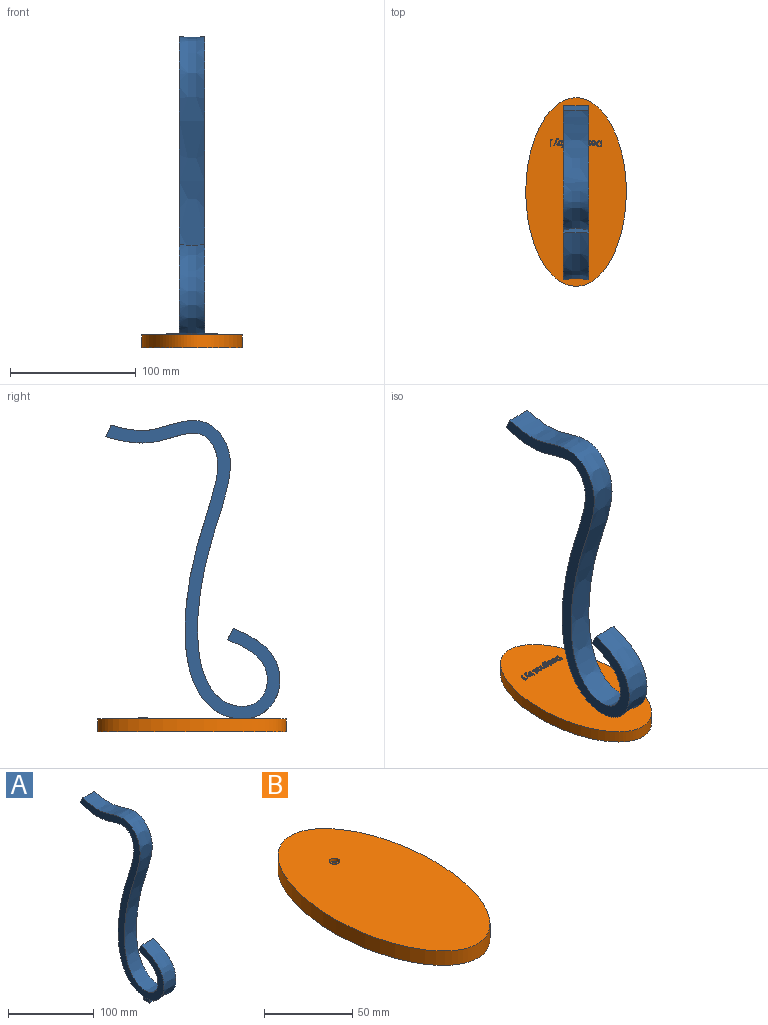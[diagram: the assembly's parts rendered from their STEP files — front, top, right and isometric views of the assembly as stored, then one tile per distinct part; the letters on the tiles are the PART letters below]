
ASSEMBLY  parts=2 mates=1
PART A: 21 faces, bbox 21x139.8x244.8 mm
  f0: plane 16.04x7.22mm, normal (0,-1,0), area 96.4mm2, adj f2,f8,f10,f11,f12,f13,f14,f15
  f1: cylinder r=1.5mm len=3.4mm, axis (0,0,-1), area 32mm2, adj f11,f14
  f2: bspline ~228.79x138.81mm, area 8693.5mm2, adj f0,f3,f5,f6,f7,f8,f9,f10
  f3: plane 238.63x139.71mm, normal (1,0,0), area 4560.6mm2, adj f2,f4,f6,f7
  f4: bspline ~228.74x126mm, area 8298.4mm2, adj f3,f5,f6,f7
  f5: plane 238.85x139.68mm, normal (-1,0,0), area 4534.9mm2, adj f2,f4,f6,f7
  f6: plane 20.02x9.13mm, normal (0,0.91,0.42), area 179.9mm2, adj f2,f3,f4,f5
  f7: plane 20.02x9mm, normal (0,0.89,0.45), area 179.9mm2, adj f2,f3,f4,f5
  f8: plane 10.05x6.7mm, normal (1,0,0), area 64.1mm2, adj f0,f2,f9,f11
  f9: plane 16.26x7.42mm, normal (0,1,0), area 111.7mm2, adj f2,f8,f10,f11
  f10: plane 10.05x6.7mm, normal (-1,0,0), area 64.1mm2, adj f0,f2,f9,f11
  f11: plane 16x10mm, normal (0,0,-1), area 152.9mm2, adj f0,f1,f8,f9,f10
  f12: plane 5.8x2.6mm, normal (-1,0,0), area 15.1mm2, adj f0,f14,f15,f16
  f13: plane 5.8x2.6mm, normal (1,0,0), area 15.1mm2, adj f0,f14,f15,f18
  f14: plane 8x6mm, normal (0,0,1), area 38.1mm2, adj f0,f1,f12,f13,f16,f17,f18
  f15: plane 8x6mm, normal (0,0,-1), area 38.1mm2, adj f0,f12,f13,f16,f17,f18,f19
  f16: plane 2.6x2.2mm, normal (-0.87,-0.5,0), area 6.6mm2, adj f12,f14,f15,f17
  f17: plane 3.46x2.6mm, normal (0,-1,0), area 9mm2, adj f14,f15,f16,f18
  f18: plane 2.6x2.2mm, normal (0.87,-0.5,0), area 6.6mm2, adj f13,f14,f15,f17
  f19: cylinder r=1.5mm len=3mm, axis (0,0,-1), area 28.3mm2, adj f15,f20
  f20: plane 3x3mm, normal (0,0,-1), area 7.1mm2, adj f19
PART B: 253 faces, bbox 80x150x11 mm
  f0: plane 150x80mm, normal (0,0,-1), area 9163.2mm2, adj f2,f3,f4,f5,f6,f17,f18,f19
  f1: cylinder r=1.5mm len=3mm, axis (0,0,1), area 18.8mm2, adj f8,f10
  f2: plane 10.8x6mm, normal (1,0,0), area 64.8mm2, adj f0,f3,f6,f8
  f3: plane 16.4x6mm, normal (0,-1,0), area 98.4mm2, adj f0,f2,f4,f8
  f4: plane 10.8x6mm, normal (-1,0,0), area 64.8mm2, adj f0,f3,f6,f8
  f5: extruded ~150x80mm, area 3697.1mm2, adj f0,f7
  f6: plane 16.4x6mm, normal (0,1,0), area 98.4mm2, adj f0,f2,f4,f8
  f7: plane 150x80mm, normal (0,0,1), area 9396.5mm2, adj f5,f9
  f8: plane 16.4x10.8mm, normal (0,0,-1), area 170.1mm2, adj f1,f2,f3,f4,f6
  f9: cylinder r=3mm len=6mm, axis (0,0,1), area 37.7mm2, adj f7,f10
  f10: plane 6x6mm, normal (0,0,1), area 21.2mm2, adj f1,f9
  f11: extruded ~1.42x1mm, area 1.5mm2, adj f12,f24,f25,f26
  f12: extruded ~1.46x1mm, area 1.6mm2, adj f11,f13,f25,f26
  f13: extruded ~1.5x1mm, area 1.6mm2, adj f12,f14,f25,f26
  f14: plane 1x0.68mm, normal (0,1,0), area 0.7mm2, adj f13,f15,f25,f26
  f15: plane 3.84x1mm, normal (-1,0,0), area 3.8mm2, adj f14,f16,f25,f26
  f16: plane 1x0.81mm, normal (0,-1,0), area 0.8mm2, adj f15,f24,f25,f26
  f17: extruded ~1.82x1mm, area 2mm2, adj f0,f18,f23,f25
  f18: extruded ~1.74x1mm, area 1.9mm2, adj f0,f17,f19,f25
  f19: extruded ~1.74x1mm, area 1.9mm2, adj f0,f18,f20,f25
  f20: plane 1.47x1mm, normal (0,1,0), area 1.5mm2, adj f0,f19,f21,f25
  f21: plane 4.81x1mm, normal (1,0,0), area 4.8mm2, adj f0,f20,f22,f25
  f22: plane 1.33x1mm, normal (0,-1,0), area 1.3mm2, adj f0,f21,f23,f25
  f23: extruded ~1.86x1mm, area 2mm2, adj f0,f17,f22,f25
  f24: extruded ~1.4x1mm, area 1.5mm2, adj f11,f16,f25,f26
  f25: plane 4.81x3.84mm, normal (0,0,-1), area 7.3mm2, adj f11,f12,f13,f14,f15,f16,f17,f18
  f26: plane 3.84x2.69mm, normal (0,0,-1), area 9.1mm2, adj f11,f12,f13,f14,f15,f16,f24
  f27: extruded ~1x0.69mm, area 0.8mm2, adj f28,f45,f46,f47
  f28: extruded ~1x0.66mm, area 0.7mm2, adj f27,f29,f46,f47
  f29: extruded ~1x0.79mm, area 0.8mm2, adj f28,f30,f46,f47
  f30: plane 1.89x1mm, normal (0,1,0), area 1.9mm2, adj f29,f45,f46,f47
  f31: extruded ~1.26x1mm, area 1.4mm2, adj f0,f32,f44,f46
  f32: extruded ~1x0.62mm, area 0.6mm2, adj f0,f31,f33,f46
  f33: extruded ~1x0.55mm, area 0.6mm2, adj f0,f32,f34,f46
  f34: plane 1x0.49mm, normal (-1,0,0), area 0.5mm2, adj f0,f33,f35,f46
  f35: extruded ~1.15x1mm, area 1.2mm2, adj f0,f34,f36,f46
  f36: extruded ~1x0.86mm, area 0.9mm2, adj f0,f35,f37,f46
  f37: extruded ~1x0.96mm, area 1mm2, adj f0,f36,f38,f46
  f38: plane 2.48x1mm, normal (0,-1,0), area 2.5mm2, adj f0,f37,f39,f46
  f39: plane 1x0.35mm, normal (-1,0,0), area 0.3mm2, adj f0,f38,f40,f46
  f40: extruded ~1.18x1mm, area 1.3mm2, adj f0,f39,f41,f46
  f41: extruded ~1.07x1mm, area 1.2mm2, adj f0,f40,f42,f46
  f42: extruded ~1.15x1mm, area 1.3mm2, adj f0,f41,f43,f46
  f43: extruded ~1.39x1mm, area 1.5mm2, adj f0,f42,f44,f46
  f44: extruded ~1.35x1mm, area 1.5mm2, adj f0,f31,f43,f46
  f45: extruded ~1x0.78mm, area 0.9mm2, adj f27,f30,f46,f47
  f46: plane 3.74x3.05mm, normal (0,0,-1), area 5.2mm2, adj f27,f28,f29,f30,f31,f32,f33,f34
  f47: plane 1.89x1.07mm, normal (0,0,-1), area 1.6mm2, adj f27,f28,f29,f30,f45
  f48: extruded ~1x0.78mm, area 0.9mm2, adj f0,f49,f72,f73
  f49: extruded ~1x0.6mm, area 0.7mm2, adj f0,f48,f50,f73
  f50: extruded ~1x0.87mm, area 1mm2, adj f0,f49,f51,f73
  f51: extruded ~1x0.63mm, area 0.7mm2, adj f0,f50,f52,f73
  f52: extruded ~1x0.24mm, area 0.3mm2, adj f0,f51,f53,f73
  f53: extruded ~1x0.25mm, area 0.3mm2, adj f0,f52,f54,f73
  f54: extruded ~1x0.34mm, area 0.4mm2, adj f0,f53,f55,f73
  f55: extruded ~1x0.59mm, area 0.6mm2, adj f0,f54,f56,f73
  f56: extruded ~1x0.98mm, area 1mm2, adj f0,f55,f57,f73
  f57: plane 1x0.44mm, normal (-0.92,-0.4,0), area 0.5mm2, adj f0,f56,f58,f73
  f58: extruded ~1.14x1mm, area 1.2mm2, adj f0,f57,f59,f73
  f59: extruded ~1x0.98mm, area 1mm2, adj f0,f58,f60,f73
  f60: extruded ~1x0.7mm, area 0.8mm2, adj f0,f59,f61,f73
  f61: extruded ~1x0.42mm, area 0.4mm2, adj f0,f60,f62,f73
  f62: extruded ~1x0.32mm, area 0.5mm2, adj f0,f61,f63,f73
  f63: extruded ~1x0.72mm, area 0.8mm2, adj f0,f62,f64,f73
  f64: extruded ~1x0.71mm, area 0.8mm2, adj f0,f63,f65,f73
  f65: extruded ~1x0.36mm, area 0.4mm2, adj f0,f64,f66,f73
  f66: extruded ~1x0.42mm, area 0.5mm2, adj f0,f65,f67,f73
  f67: extruded ~1x0.66mm, area 0.7mm2, adj f0,f66,f68,f73
  f68: extruded ~1x0.57mm, area 0.6mm2, adj f0,f67,f69,f73
  f69: extruded ~1x0.56mm, area 0.6mm2, adj f0,f68,f70,f73
  f70: plane 1x0.51mm, normal (1,0,0), area 0.5mm2, adj f0,f69,f71,f73
  f71: extruded ~1.12x1mm, area 1.2mm2, adj f0,f70,f72,f73
  f72: extruded ~1.05x1mm, area 1.1mm2, adj f0,f48,f71,f73
  f73: plane 3.74x2.56mm, normal (0,0,-1), area 4mm2, adj f48,f49,f50,f51,f52,f53,f54,f55
  f74: plane 1x0.55mm, normal (0,-1,0), area 0.5mm2, adj f0,f75,f77,f78
  f75: plane 3.61x1mm, normal (-1,0,0), area 3.6mm2, adj f0,f74,f76,f78
  f76: plane 1x0.55mm, normal (0,1,0), area 0.5mm2, adj f0,f75,f77,f78
  f77: plane 3.61x1mm, normal (1,0,0), area 3.6mm2, adj f0,f74,f76,f78
  f78: plane 3.61x0.55mm, normal (0,0,-1), area 2mm2, adj f74,f75,f76,f77
  f79: extruded ~1x0.28mm, area 0.3mm2, adj f0,f80,f86,f87
  f80: extruded ~1x0.28mm, area 0.3mm2, adj f0,f79,f81,f87
  f81: extruded ~1x0.23mm, area 0.3mm2, adj f0,f80,f82,f87
  f82: extruded ~1x0.23mm, area 0.3mm2, adj f0,f81,f83,f87
  f83: extruded ~1x0.28mm, area 0.3mm2, adj f0,f82,f84,f87
  f84: extruded ~1x0.27mm, area 0.3mm2, adj f0,f83,f85,f87
  f85: extruded ~1x0.23mm, area 0.2mm2, adj f0,f84,f86,f87
  f86: extruded ~1x0.23mm, area 0.3mm2, adj f0,f79,f85,f87
  f87: plane 0.73x0.65mm, normal (0,0,-1), area 0.4mm2, adj f79,f80,f81,f82,f83,f84,f85,f86
  f88: extruded ~1x0.57mm, area 0.6mm2, adj f89,f131,f132,f134
  f89: extruded ~1x0.62mm, area 0.7mm2, adj f88,f90,f132,f134
  f90: extruded ~1x0.59mm, area 0.6mm2, adj f89,f91,f132,f134
  f91: extruded ~1x0.81mm, area 1.3mm2, adj f90,f92,f132,f134
  f92: extruded ~1x0.8mm, area 1.3mm2, adj f91,f131,f132,f134
  f93: extruded ~1x0.44mm, area 0.5mm2, adj f94,f129,f132,f133
  f94: extruded ~1x0.51mm, area 0.6mm2, adj f93,f95,f132,f133
  f95: extruded ~1x0.58mm, area 0.6mm2, adj f94,f96,f132,f133
  f96: plane 1x0.66mm, normal (0,-1,0), area 0.7mm2, adj f95,f97,f132,f133
  f97: extruded ~1x0.68mm, area 0.7mm2, adj f96,f98,f132,f133
  f98: extruded ~1x0.41mm, area 0.5mm2, adj f97,f99,f132,f133
  f99: extruded ~1x0.56mm, area 0.7mm2, adj f98,f100,f132,f133
  f100: extruded ~1.02x1mm, area 1.1mm2, adj f99,f129,f132,f133
  f101: plane 1x0.35mm, normal (-1,0,0), area 0.3mm2, adj f0,f102,f130,f132
  f102: plane 1.25x1mm, normal (0,1,0), area 1.2mm2, adj f0,f101,f103,f132
  f103: extruded ~1x0.51mm, area 0.5mm2, adj f0,f102,f104,f132
  f104: extruded ~1.01x1mm, area 1.1mm2, adj f0,f103,f105,f132
  f105: extruded ~1x0.91mm, area 1mm2, adj f0,f104,f106,f132
  f106: extruded ~1x0.63mm, area 0.7mm2, adj f0,f105,f107,f132
  f107: extruded ~1x0.46mm, area 0.6mm2, adj f0,f106,f108,f132
  f108: extruded ~1x0.33mm, area 0.4mm2, adj f0,f107,f109,f132
  f109: extruded ~1x0.35mm, area 0.4mm2, adj f0,f108,f110,f132
  f110: extruded ~1x0.31mm, area 0.3mm2, adj f0,f109,f111,f132
  f111: extruded ~1x0.23mm, area 0.3mm2, adj f0,f110,f112,f132
  f112: extruded ~1x0.59mm, area 0.7mm2, adj f0,f111,f113,f132
  f113: extruded ~1x0.57mm, area 0.6mm2, adj f0,f112,f114,f132
  f114: extruded ~1x0.74mm, area 0.9mm2, adj f0,f113,f115,f132
  f115: extruded ~1.09x1mm, area 1.1mm2, adj f0,f114,f116,f132
  f116: extruded ~1.4x1mm, area 1.5mm2, adj f0,f115,f117,f132
  f117: extruded ~1x0.91mm, area 1.1mm2, adj f0,f116,f118,f132
  f118: extruded ~1x0.72mm, area 0.8mm2, adj f0,f117,f119,f132
  f119: extruded ~1x0.9mm, area 1mm2, adj f0,f118,f120,f132
  f120: plane 1x0.64mm, normal (0,1,0), area 0.6mm2, adj f0,f119,f121,f132
  f121: extruded ~1x0.42mm, area 0.4mm2, adj f0,f120,f122,f132
  f122: extruded ~1x0.22mm, area 0.3mm2, adj f0,f121,f123,f132
  f123: extruded ~1x0.46mm, area 0.6mm2, adj f0,f122,f124,f132
  f124: extruded ~1x0.3mm, area 0.3mm2, adj f0,f123,f125,f132
  f125: extruded ~1x0.99mm, area 1.1mm2, adj f0,f124,f126,f132
  f126: extruded ~1x0.85mm, area 1mm2, adj f0,f125,f127,f132
  f127: extruded ~1x0.42mm, area 0.4mm2, adj f0,f126,f128,f132
  f128: extruded ~1x0.3mm, area 0.3mm2, adj f0,f127,f130,f132
  f129: extruded ~1x0.71mm, area 0.7mm2, adj f93,f100,f132,f133
  f130: plane 1x0.67mm, normal (-0.12,-0.99,0), area 0.7mm2, adj f0,f101,f128,f132
  f131: extruded ~1x0.6mm, area 0.6mm2, adj f88,f92,f132,f134
  f132: plane 5.29x3.4mm, normal (0,0,-1), area 7.4mm2, adj f88,f89,f90,f91,f92,f93,f94,f95
  f133: plane 2.3x1.28mm, normal (0,0,-1), area 2.5mm2, adj f93,f94,f95,f96,f97,f98,f99,f100
  f134: plane 1.61x1.59mm, normal (0,0,-1), area 2.1mm2, adj f88,f89,f90,f91,f92,f131
  f135: plane 2.33x1mm, normal (1,0,0), area 2.3mm2, adj f0,f136,f151,f152
  f136: plane 1x0.55mm, normal (0,-1,0), area 0.5mm2, adj f0,f135,f137,f152
  f137: plane 2.35x1mm, normal (-1,0,0), area 2.4mm2, adj f0,f136,f138,f152
  f138: extruded ~1.01x1mm, area 1.1mm2, adj f0,f137,f139,f152
  f139: extruded ~1x0.98mm, area 1.1mm2, adj f0,f138,f140,f152
  f140: extruded ~1x0.67mm, area 0.7mm2, adj f0,f139,f141,f152
  f141: extruded ~1x0.47mm, area 0.6mm2, adj f0,f140,f142,f152
  f142: plane 1x0.03mm, normal (0,1,0), area 0mm2, adj f0,f141,f143,f152
  f143: plane 1x0.49mm, normal (-0.98,0.18,0), area 0.5mm2, adj f0,f142,f144,f152
  f144: plane 1x0.44mm, normal (0,1,0), area 0.4mm2, adj f0,f143,f145,f152
  f145: plane 3.61x1mm, normal (1,0,0), area 3.6mm2, adj f0,f144,f146,f152
  f146: plane 1x0.55mm, normal (0,-1,0), area 0.5mm2, adj f0,f145,f147,f152
  f147: plane 1.89x1mm, normal (-1,0,0), area 1.9mm2, adj f0,f146,f148,f152
  f148: extruded ~1.01x1mm, area 1.1mm2, adj f0,f147,f149,f152
  f149: extruded ~1x0.83mm, area 0.9mm2, adj f0,f148,f150,f152
  f150: extruded ~1x0.63mm, area 0.7mm2, adj f0,f149,f151,f152
  f151: extruded ~1x0.66mm, area 0.7mm2, adj f0,f135,f150,f152
  f152: plane 3.67x3.01mm, normal (0,0,-1), area 4.7mm2, adj f135,f136,f137,f138,f139,f140,f141,f142
  f153: extruded ~1x0.69mm, area 0.8mm2, adj f154,f171,f172,f173
  f154: extruded ~1x0.66mm, area 0.7mm2, adj f153,f155,f172,f173
  f155: extruded ~1x0.79mm, area 0.8mm2, adj f154,f156,f172,f173
  f156: plane 1.89x1mm, normal (0,1,0), area 1.9mm2, adj f155,f171,f172,f173
  f157: extruded ~1.26x1mm, area 1.4mm2, adj f0,f158,f170,f172
  f158: extruded ~1x0.62mm, area 0.6mm2, adj f0,f157,f159,f172
  f159: extruded ~1x0.55mm, area 0.6mm2, adj f0,f158,f160,f172
  f160: plane 1x0.49mm, normal (-1,0,0), area 0.5mm2, adj f0,f159,f161,f172
  f161: extruded ~1.15x1mm, area 1.2mm2, adj f0,f160,f162,f172
  f162: extruded ~1x0.86mm, area 0.9mm2, adj f0,f161,f163,f172
  f163: extruded ~1x0.96mm, area 1mm2, adj f0,f162,f164,f172
  f164: plane 2.48x1mm, normal (0,-1,0), area 2.5mm2, adj f0,f163,f165,f172
  f165: plane 1x0.35mm, normal (-1,0,0), area 0.3mm2, adj f0,f164,f166,f172
  f166: extruded ~1.18x1mm, area 1.3mm2, adj f0,f165,f167,f172
  f167: extruded ~1.07x1mm, area 1.2mm2, adj f0,f166,f168,f172
  f168: extruded ~1.15x1mm, area 1.3mm2, adj f0,f167,f169,f172
  f169: extruded ~1.39x1mm, area 1.5mm2, adj f0,f168,f170,f172
  f170: extruded ~1.35x1mm, area 1.5mm2, adj f0,f157,f169,f172
  f171: extruded ~1x0.78mm, area 0.9mm2, adj f153,f156,f172,f173
  f172: plane 3.74x3.05mm, normal (0,0,-1), area 5.2mm2, adj f153,f154,f155,f156,f157,f158,f159,f160
  f173: plane 1.89x1.07mm, normal (0,0,-1), area 1.6mm2, adj f153,f154,f155,f156,f171
  f174: extruded ~1x0.81mm, area 0.9mm2, adj f175,f197,f198,f199
  f175: extruded ~1x0.74mm, area 0.9mm2, adj f174,f176,f198,f199
  f176: extruded ~1.04x1mm, area 1.1mm2, adj f175,f177,f198,f199
  f177: extruded ~1.05x1mm, area 1.1mm2, adj f176,f178,f198,f199
  f178: extruded ~1x0.74mm, area 0.9mm2, adj f177,f179,f198,f199
  f179: extruded ~1x0.81mm, area 0.9mm2, adj f178,f180,f198,f199
  f180: extruded ~1.09x1mm, area 1.1mm2, adj f179,f181,f198,f199
  f181: plane 1x0.11mm, normal (1,0,0), area 0.1mm2, adj f180,f197,f198,f199
  f182: plane 1x0.03mm, normal (0,-1,0), area 0mm2, adj f0,f183,f196,f198
  f183: plane 1x0.48mm, normal (0.99,-0.15,0), area 0.5mm2, adj f0,f182,f184,f198
  f184: plane 1x0.44mm, normal (0,-1,0), area 0.4mm2, adj f0,f183,f185,f198
  f185: plane 5.12x1mm, normal (-1,0,0), area 5.1mm2, adj f0,f184,f186,f198
  f186: plane 1x0.55mm, normal (0,1,0), area 0.5mm2, adj f0,f185,f187,f198
  f187: plane 1.47x1mm, normal (1,0,0), area 1.5mm2, adj f0,f186,f188,f198
  f188: plane 1x0.25mm, normal (1,-0.05,0), area 0.3mm2, adj f0,f187,f189,f198
  f189: plane 1x0.26mm, normal (1,-0.09,0), area 0.3mm2, adj f0,f188,f190,f198
  f190: plane 1x0.04mm, normal (0,1,0), area 0mm2, adj f0,f189,f191,f198
  f191: extruded ~1.13x1mm, area 1.3mm2, adj f0,f190,f192,f198
  f192: extruded ~1.1x1mm, area 1.2mm2, adj f0,f191,f193,f198
  f193: extruded ~1.39x1mm, area 1.5mm2, adj f0,f192,f194,f198
  f194: extruded ~1.38x1mm, area 1.5mm2, adj f0,f193,f195,f198
  f195: extruded ~1.1x1mm, area 1.2mm2, adj f0,f194,f196,f198
  f196: extruded ~1.13x1mm, area 1.3mm2, adj f0,f182,f195,f198
  f197: extruded ~1x0.98mm, area 1mm2, adj f174,f181,f198,f199
  f198: plane 5.19x3.17mm, normal (0,0,-1), area 6.3mm2, adj f174,f175,f176,f177,f178,f179,f180,f181
  f199: plane 2.82x2.06mm, normal (0,0,-1), area 4.9mm2, adj f174,f175,f176,f177,f178,f179,f180,f181
  f200: extruded ~1x0.81mm, area 0.9mm2, adj f201,f222,f223,f224
  f201: extruded ~1x0.76mm, area 0.9mm2, adj f200,f202,f223,f224
  f202: extruded ~1.05x1mm, area 1.1mm2, adj f201,f203,f223,f224
  f203: extruded ~1.05x1mm, area 1.1mm2, adj f202,f204,f223,f224
  f204: extruded ~1x0.75mm, area 0.9mm2, adj f203,f205,f223,f224
  f205: extruded ~1x0.81mm, area 0.9mm2, adj f204,f206,f223,f224
  f206: extruded ~1.09x1mm, area 1.1mm2, adj f205,f222,f223,f224
  f207: extruded ~1.1x1mm, area 1.2mm2, adj f0,f208,f221,f223
  f208: extruded ~1.13x1mm, area 1.3mm2, adj f0,f207,f209,f223
  f209: plane 1x0.03mm, normal (0,1,0), area 0mm2, adj f0,f208,f210,f223
  f210: extruded ~1x0.75mm, area 0.8mm2, adj f0,f209,f211,f223
  f211: plane 1.24x1mm, normal (-1,0,0), area 1.2mm2, adj f0,f210,f212,f223
  f212: plane 1x0.55mm, normal (0,1,0), area 0.5mm2, adj f0,f211,f213,f223
  f213: plane 5.12x1mm, normal (1,0,0), area 5.1mm2, adj f0,f212,f214,f223
  f214: plane 1x0.39mm, normal (0,-1,0), area 0.4mm2, adj f0,f213,f215,f223
  f215: plane 1x0.46mm, normal (-0.97,-0.24,0), area 0.5mm2, adj f0,f214,f216,f223
  f216: plane 1x0.04mm, normal (0,-1,0), area 0mm2, adj f0,f215,f217,f223
  f217: extruded ~1x0.49mm, area 0.6mm2, adj f0,f216,f218,f223
  f218: extruded ~1x0.64mm, area 0.7mm2, adj f0,f217,f219,f223
  f219: extruded ~1.1x1mm, area 1.3mm2, adj f0,f218,f220,f223
  f220: extruded ~1.38x1mm, area 1.5mm2, adj f0,f219,f221,f223
  f221: extruded ~1.37x1mm, area 1.5mm2, adj f0,f207,f220,f223
  f222: extruded ~1.08x1mm, area 1.1mm2, adj f200,f206,f223,f224
  f223: plane 5.19x3.18mm, normal (0,0,-1), area 6.3mm2, adj f200,f201,f202,f203,f204,f205,f206,f207
  f224: plane 2.82x2.06mm, normal (0,0,-1), area 4.9mm2, adj f200,f201,f202,f203,f204,f205,f206,f222
  f225: plane 1x0.59mm, normal (0,1,0), area 0.6mm2, adj f0,f226,f240,f241
  f226: plane 3.63x1.46mm, normal (0.93,-0.37,0), area 3.9mm2, adj f0,f225,f227,f241
  f227: plane 1x0.51mm, normal (0.93,0.37,0), area 0.6mm2, adj f0,f226,f228,f241
  f228: extruded ~1x0.8mm, area 1.1mm2, adj f0,f227,f229,f241
  f229: extruded ~1x0.4mm, area 0.4mm2, adj f0,f228,f230,f241
  f230: plane 1x0.44mm, normal (1,0,0), area 0.4mm2, adj f0,f229,f231,f241
  f231: extruded ~1x0.49mm, area 0.5mm2, adj f0,f230,f232,f241
  f232: extruded ~1x0.76mm, area 0.8mm2, adj f0,f231,f233,f241
  f233: extruded ~1x0.86mm, area 1mm2, adj f0,f232,f234,f241
  f234: plane 4.11x1.55mm, normal (-0.94,-0.35,0), area 4.4mm2, adj f0,f233,f235,f241
  f235: plane 1x0.59mm, normal (0,1,0), area 0.6mm2, adj f0,f234,f236,f241
  f236: extruded ~2.5x1mm, area 2.7mm2, adj f0,f235,f237,f241
  f237: extruded ~1x0.58mm, area 0.6mm2, adj f0,f236,f238,f241
  f238: plane 1x0.03mm, normal (0,1,0), area 0mm2, adj f0,f237,f239,f241
  f239: extruded ~1.02x1mm, area 1.1mm2, adj f0,f238,f240,f241
  f240: plane 2.06x1mm, normal (-0.93,0.36,0), area 2.2mm2, adj f0,f225,f239,f241
  f241: plane 5.23x3.38mm, normal (0,0,-1), area 5mm2, adj f225,f226,f227,f228,f229,f230,f231,f232
  f242: extruded ~1x0.49mm, area 0.5mm2, adj f0,f243,f251,f252
  f243: extruded ~1x0.91mm, area 1mm2, adj f0,f242,f244,f252
  f244: extruded ~1x0.97mm, area 1mm2, adj f0,f243,f245,f252
  f245: plane 4.76x1mm, normal (-1,0,0), area 4.8mm2, adj f0,f244,f246,f252
  f246: plane 1x0.56mm, normal (0,1,0), area 0.6mm2, adj f0,f245,f247,f252
  f247: plane 4.81x1mm, normal (1,0,0), area 4.8mm2, adj f0,f246,f248,f252
  f248: extruded ~1x0.57mm, area 0.6mm2, adj f0,f247,f249,f252
  f249: extruded ~1x0.5mm, area 0.6mm2, adj f0,f248,f250,f252
  f250: extruded ~1x0.49mm, area 0.5mm2, adj f0,f249,f251,f252
  f251: plane 1x0.48mm, normal (1,0,0), area 0.5mm2, adj f0,f242,f250,f252
  f252: plane 6.08x1.71mm, normal (0,0,-1), area 3.8mm2, adj f242,f243,f244,f245,f246,f247,f248,f249
PLACE A t=(-139.01,-133.4,165.71)mm
PLACE B rot(axis=(1,0,0),180deg) t=(-129.01,-134.44,118.09)mm
MATE fastened A.f1 <-> B.f9  axis (0,0,-1) through (-129.01,-174.04,122.09)mm
